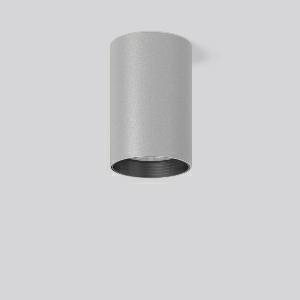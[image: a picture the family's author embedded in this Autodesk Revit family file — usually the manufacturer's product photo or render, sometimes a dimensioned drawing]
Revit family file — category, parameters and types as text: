
# Revit family: heledon_maxi_a_931222_004_1_0431
name_source: partatom
category: Lighting Fixtures
units: mm (PartAtom-declared; Revit-internal decimal feet)

## family parameters
Cut with Voids When Loaded = No
Host = Face
Light Source = No
Part Type = Normal
Room Calculation Point = No
Round Connector Dimension = Use Diameter
Shared = No

## types (1)
- HELEDON maxi A (1 x LED Modul 940, 2950 lm, 4000)
    Apparent Load = 25 VA
    Approval mark = CE
    CIE Flux Codes = 96 100 100 100 100
    Color Rendering = 92
    Color Temperature = 4000
    Default Elevation = 1800 mm
    Description = Series: HELEDON maxi
Cylindrical surface-mounted downlight. Housing: die-cast aluminium, powder-coated. Internal ceiling frame polycarbonate with bayonet mounting. Black plastic ring and recessed LED to prevent glare from the side. Optical assembly with lens made of plastic (polycarbonate) for the best homogeneous light distribution - can be changed without tools. Best colour rendering index Ra>90. Suitable for Ceiling mounting. Easy installation with a separate ceiling frame with bayonet mounting and plug connection. Driver integrated. Connected via plug-in connector. High quality converter without flickering and stroboscopic effect. The following accessories can be mounted without use of tools: interchangeable lenses, decorative glasses, honeycomb louvre, clear and frosted diffusers, white interchangeable plastic ring. 
Colour: silver
Diameter: 123 mm
Height: 183 mm
Lamp: LED
Socket: without socket
Colour temperature: 4000K
Colour rendering index (CRI): 92
System power: 25 W
Rated luminous flux: 2950 lm
Luminous efficiency: 118 lm/W
Control gear: Regulated power supply
Protection class: I
Type of protection: IP 20
    Height = 183 mm
    Lamp = 1 x LED Modul 940
    Lamp Light Flux = 2950 lm
    Lamp count = 1
    Length = 123 mm
    Lifetime = 50000 h
    Luminous efficacy = 118 lm/W
    Manufacturer = RZB
    ModVariant = No
    Model = 931222.004.1
    Mounting Place = Ceiling
    Mounting Type = Surface mounted
    Number of Poles = 1
    OnlyDefault = Yes
    Power Factor = 1
    Product Name = HELEDON maxi A
    Product group = Surface mounted downlights
    ProductGroupID = 302
    Protection Class = Protection class I
    Protection Degree = IP 20
    RLX_Detail_Level = 1
    RLX_Emergency_Light_Flux = 0 lm
    RLX_Emergency_Type = 0
    RLX_Emergency_Type_DB = No
    RlxData = <blob elided: 98905 chars, md5=4ea7749f>
    Socket = socket
    Standby Power = 0 W
    System Light Flux = 2950 lm
    System Power = 25 W
    Type Comments = Product without accessories
    Type Image = 931193.004.jpg
    URL = http://relux.com
    VarID = ---
    Voltage = 230 V
    Voltage Range = 220-240 V
    Weight = 0.00 kg
    Width = 0 mm  [stored 0 ft]

note: [stored X ft] marks values corroborated as IEEE doubles in the binary element streams (Revit-internal decimal feet)

## geometry (parser evidence)
native form markers: Blend x4, Sweep x9
no freeform markers — native parametric forms only
